# Revit family: VLGFP1502-xxxWS8xxExxxx
name_source: partatom
category: Oprawy oświetleniowe
revit_build: Autodesk Revit 2017 (Build: 20190508_0315(x64)
units: mm (PartAtom-declared; Revit-internal decimal feet)

## family parameters
Numer OmniClass = 23.80.70.11
Obiekt nadrzędny = Powierzchnia
Punkt obliczania pomieszczeń = Nie
Tnij formami wycięć po wczytaniu = Nie
Typ części = Normalny
Tytuł OmniClass = Luminaries for Internal Lighting
Współdzielony = Nie
Wymiar okrągłego złącza = Użyj średnicy
Źródło światła = Tak

## types (15) — shared parameters
Emituj kształt widoczny w renderingu = Nie
Emituj z długości prostokąta = 63 mm  [stored 0.206693 ft]
Emituj z szerokości prostokąta = 1469 mm  [stored 4.81955 ft]
Filtr koloru = 16777215
Kod zespołu = D5020200
Lampa = LED
Odchylenie kierunku = 90.00°
Plik sieci fotometrycznej = VLGFP1501-5NDWS840E0750.IES
Producent = RIDI Leuchten GmbH
URL = www.ridi.de
Zmiana temperatury barwowej przyciemniania lampy = <Brak>
brand = RIDI
conformity mark = CE
electrical safety class = 1
height = 66 mm  [stored 0.216535 ft]
ingress protection (IP) code = IP54
length = 1500 mm  [stored 4.92126 ft]
nominal frequency = 50-60Hz
nominal voltage = 230
voltage type (AC, DC, UC) = AC
weight = 1.9 kg
width = 67 mm
zero-valued in all types: Domyślna rzędna

## per-type parameters (varying)
| type | Model | Obciążenie pozorne | product name | rated input power |
| VLGFP1502-5NDWS840E1400 | 1551018 | 100 VA | VLGFP1502-5NDWS840E1400 | 100 |
| VLGFP1502-7DAWS840E1400 | 1561018 | 100 VA | VLGFP1502-7DAWS840E1400 | 100 |
| VLGFP1502-5NDWS840E1600 | 1551092 | 121 VA | VLGFP1502-5NDWS840E1600 | 121 |
| VLGFP1502-7DAWS840E1600 | 1561092 | 121 VA | VLGFP1502-7DAWS840E1600 | 121 |
| VLGFP1502-5NDWS840E1500-RF | 1551128 | 100 VA | VLGFP1502-5NDWS840E1600 | 100 |
| VLGFP1502-5NDWS850E1400 | 1551050 | 100 VA | VLGFP1502-5NDWS850E1400 | 100 |
| VLGFP1502-7DAWS850E1400 | 1561050 | 100 VA | VLGFP1502-7DAWS850E1400 | 100 |
| VLGFP1502-5NDWS850E1700 | 1551098 | 121 VA | VLGFP1502-5NDWS850E1700 | 121 |
| VLGFP1502-7DAWS850E1700 | 1561098 | 121 VA | VLGFP1502-7DAWS850E1700 | 121 |
| VLGFP1502-5NDWS850E1500-RF | 1551129 | 100 VA | VLGFP1502-5NDWS850E1500-RF | 100 |
| VLGFP1502-5NDWS865E1400 | 1551063 | 100 VA | VLGFP1502-5NDWS865E1400 | 100 |
| VLGFP1502-5NDWS865E1600 | 1551102 | 121 VA | VLGFP1502-5NDWS865E1600 | 121 |
| VLGFP1502-7DAWS865E1600 | 1561102 | 121 VA | VLGFP1502-7DAWS865E1600 | 121 |
| VLGFP1502-5NDWS865E1500-RF | 1551130 | 100 VA | VLGFP1502-5NDWS865E1500-RF | 100 |
| VLGFP1502-7DAWS865E1400 | 1561063 | 100 VA | VLGFP1502-7DAWS865E1400 | 100 |

note: [stored X ft] marks values corroborated as IEEE doubles in the binary element streams (Revit-internal decimal feet)
